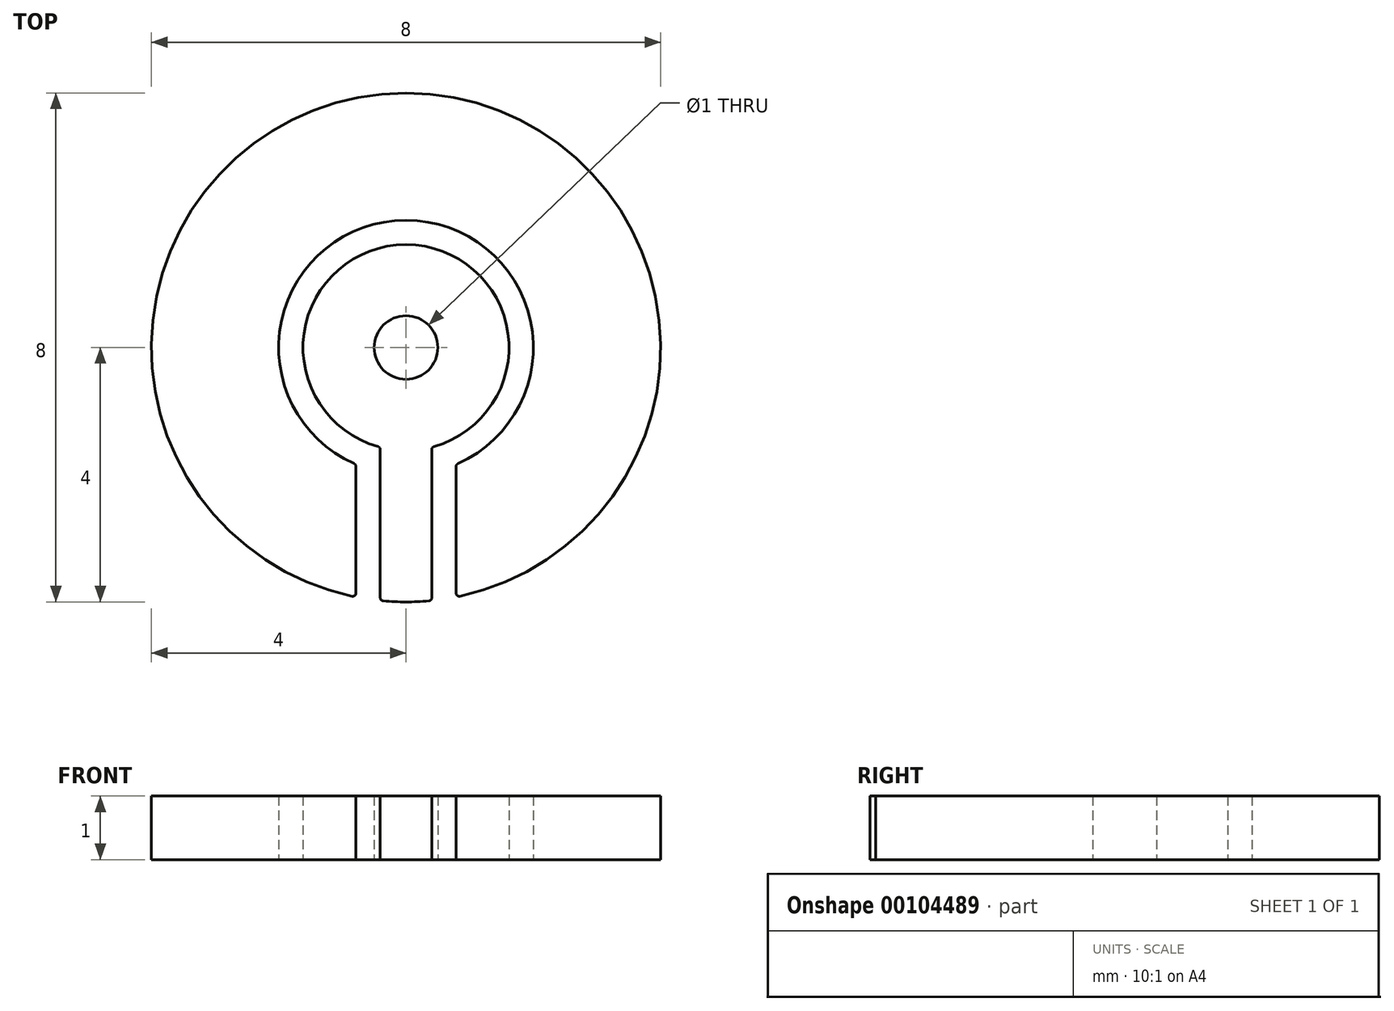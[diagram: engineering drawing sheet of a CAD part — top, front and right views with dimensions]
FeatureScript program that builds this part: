
annotation { "Feature Type Name" : "Feature", "Feature Type Description" : "" }
export const myFeature = defineFeature(function(context is Context, id is Id, definition is map)
    precondition{}
    {
        {
            var Q0;
            Q0=qCreatedBy(makeId("Top.planeOp"),FACE);
            var sketch = newSketch(context, id + "F0", { "sketchPlane" : qUnion([Q0])});
            skCircle(sketch, "E0", {"center": v(0, 0) * mm, "radius": 0.5 * mm});
            skArc(sketch, "E1", {"start": v(0.82, -1.83) * mm, "mid": v(0, 2) * mm, "end": v(-0.82, -1.83) * mm});
            skLineSegment(sketch, "E2.left", {"start": v(0.79, -3.86) * mm, "end": v(0.79, -1.87) * mm});
            skLineSegment(sketch, "E2.right", {"start": v(-0.79, -3.86) * mm, "end": v(-0.79, -1.87) * mm});
            skPoint(sketch, "E2.middle", {"position": v(0, -2.1) * mm});
            skArc(sketch, "E3", {"start": v(0.44, -1.56) * mm, "mid": v(0, 1.62) * mm, "end": v(-0.44, -1.56) * mm});
            skLineSegment(sketch, "E4.left", {"start": v(0.4, -3.93) * mm, "end": v(0.4, -1.6) * mm});
            skLineSegment(sketch, "E4.right", {"start": v(-0.4, -3.93) * mm, "end": v(-0.4, -1.6) * mm});
            skPoint(sketch, "E4.middle", {"position": v(0, -2.59) * mm});
            skArc(sketch, "E5", {"start": v(-0.36, -3.98) * mm, "mid": v(0, -4) * mm, "end": v(0.36, -3.98) * mm});
            skArc(sketch, "E6.trimOffspring", {"start": v(0.85, -3.9) * mm, "mid": v(0, 4) * mm, "end": v(-0.85, -3.9) * mm});
            skPoint(sketch, "E7.visualSharp", {"position": v(-0.4, -1.57) * mm});
            skArc(sketch, "E7.filletArc", {"start": v(-0.4, -1.6) * mm, "mid": v(-0.41, -1.57) * mm, "end": v(-0.44, -1.56) * mm});
            skPoint(sketch, "E8.visualSharp", {"position": v(0.4, -1.57) * mm});
            skArc(sketch, "E8.filletArc", {"start": v(0.44, -1.56) * mm, "mid": v(0.41, -1.57) * mm, "end": v(0.4, -1.6) * mm});
            skPoint(sketch, "E9.visualSharp", {"position": v(0.79, -1.84) * mm});
            skArc(sketch, "E9.filletArc", {"start": v(0.82, -1.83) * mm, "mid": v(0.8, -1.84) * mm, "end": v(0.79, -1.87) * mm});
            skPoint(sketch, "E10.visualSharp", {"position": v(0.79, -3.92) * mm});
            skArc(sketch, "E10.filletArc", {"start": v(0.79, -3.86) * mm, "mid": v(0.8, -3.9) * mm, "end": v(0.85, -3.9) * mm});
            skPoint(sketch, "E11.visualSharp", {"position": v(0.4, -3.98) * mm});
            skArc(sketch, "E11.filletArc", {"start": v(0.36, -3.98) * mm, "mid": v(0.4, -3.97) * mm, "end": v(0.4, -3.93) * mm});
            skPoint(sketch, "E12.visualSharp", {"position": v(-0.4, -3.98) * mm});
            skArc(sketch, "E12.filletArc", {"start": v(-0.4, -3.93) * mm, "mid": v(-0.4, -3.97) * mm, "end": v(-0.36, -3.98) * mm});
            skPoint(sketch, "E13.visualSharp", {"position": v(-0.79, -3.92) * mm});
            skArc(sketch, "E13.filletArc", {"start": v(-0.85, -3.9) * mm, "mid": v(-0.8, -3.9) * mm, "end": v(-0.79, -3.86) * mm});
            skPoint(sketch, "E14.visualSharp", {"position": v(-0.79, -1.84) * mm});
            skArc(sketch, "E14.filletArc", {"start": v(-0.79, -1.87) * mm, "mid": v(-0.8, -1.84) * mm, "end": v(-0.82, -1.83) * mm});
            skCircle(sketch, "E15", {"center": v(0, 0) * mm, "radius": 9.84 * mm});
            skSolve(sketch);
        }
        {
            var Q0;
            Q0=makeQuery(id+"F0.imprint","IMPRINT",FACE,{"disambiguationData":[TD([[makeQuery(id+"F0.imprint","IMPRINT",EDGE,{"derivedFrom":sQuery(id+"F0.wireOp",EDGE,"E1")}),-1.0]])]});
            var Q1;
            Q1=makeQuery(id+"F0.imprint","IMPRINT",FACE,{"disambiguationData":[TD([[makeQuery(id+"F0.imprint","IMPRINT",EDGE,{"derivedFrom":sQuery(id+"F0.wireOp",EDGE,"E0")}),-1.0]])]});
            extrude(context, id + "F1", {"entities" : qUnion([Q0, Q1]), "depth" : 1 * mm});
        }
    });
